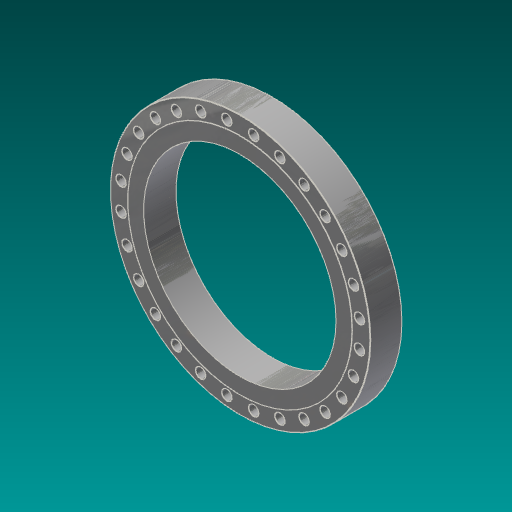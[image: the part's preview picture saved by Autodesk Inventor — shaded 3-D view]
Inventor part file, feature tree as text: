
AUTODESK INVENTOR PART (.ipt)
format: ipt  version: 2017.3 (Build 213257000, 257)  size: 274,432 bytes
history: native  units: in
note: dims shown in document units (in); Inventor stores cm internally (conversion verified against a paired STEP export)
features: sketch x3, extrude x2, chamfer x2, hole x1, pattern_circular x1
ambient origin geometry x8: Origin, YZ Plane, XZ Plane, XY Plane, X Axis, Y Axis, Z Axis, Center Point
bodies: Solid1 (feature_tree)
feature tree (9):
  extrude  "Extrusion1"  Depth=30.875in
  hole  "Hole1"  [1 undecoded]
  chamfer  "Chamfer1"  Distance=11.0236in Angle=360.0deg
  pattern_circular  "Circular Pattern1"  Angle=45.0deg  [1 undecoded]
  extrude  "Extrusion2"  Depth=0.0625in TaperAngle=45.0deg
  chamfer  "Chamfer2"  Distance=36.0in
  sketch  "Sketch1"  dims[d0=41.75in d1=30.875in]
  sketch  "Sketch2"  dims[d2=5.125in d3=0.0in d4=38.5in]
  sketch  "Sketch3"  dims[d5=0.0442in d6=1.625in d7=0.75in d8=0.375in d9=0.25in d10=0.5635in d11=1.0in d12=0.8108in d13=11.0236in d14=360.0deg d16=0.0312in d17=0.125in d18=45.0deg d19=0.0625in d20=0.125in d21=45.0deg d25=36.0in d26=0.0625in d27=0.0in]
note: 2 required parameter values undecoded (feature->parameter linkage not recoverable at this tier; creation-order binding heuristic only, values carry confidence <= 0.55)
